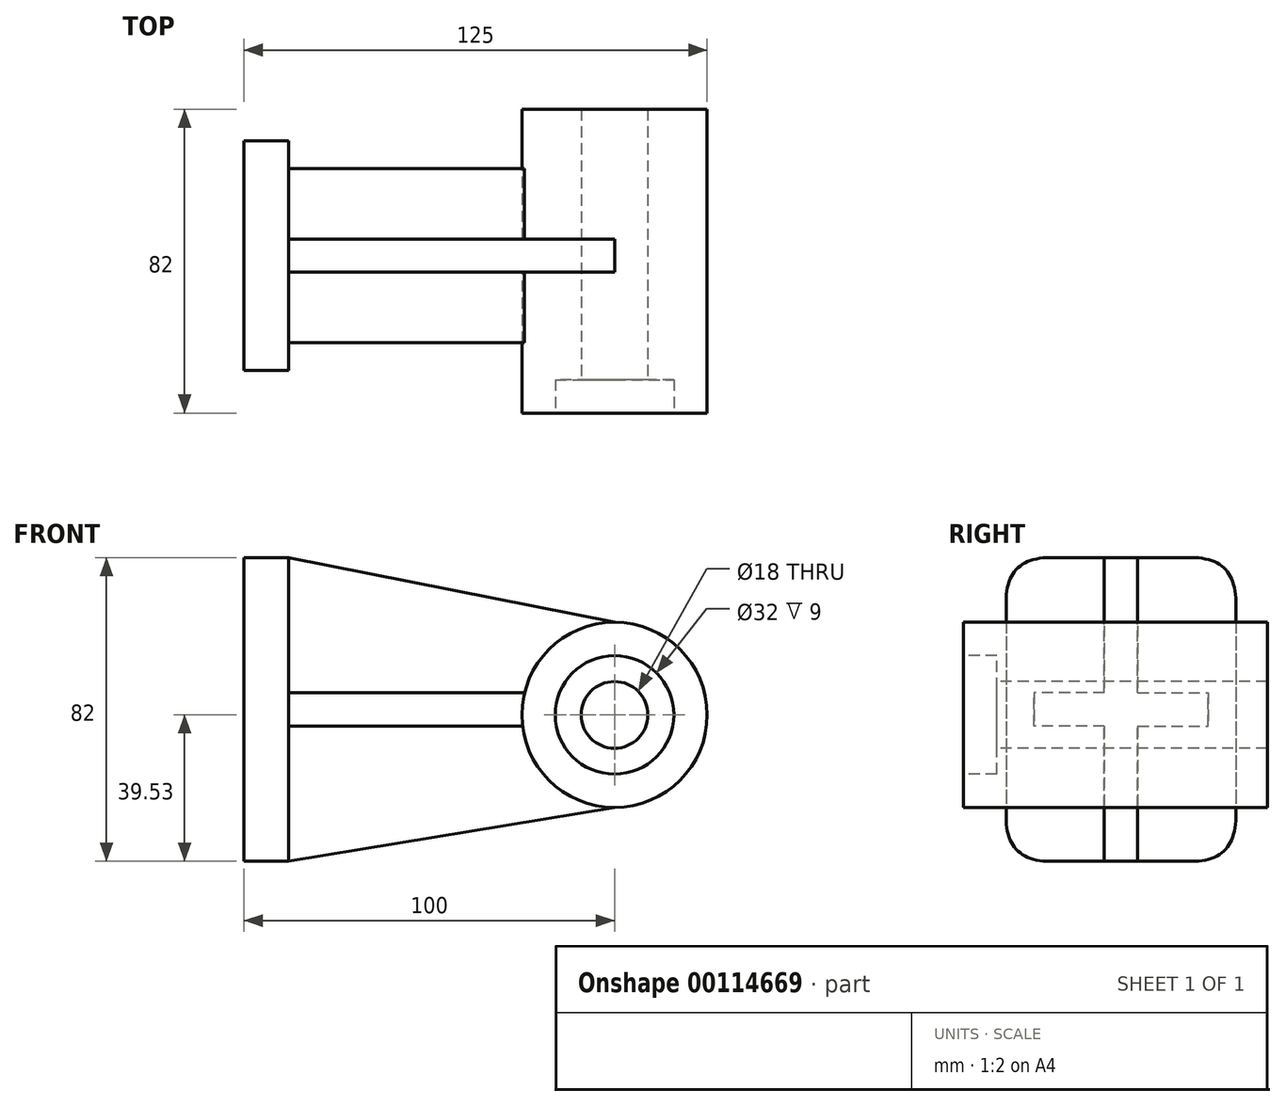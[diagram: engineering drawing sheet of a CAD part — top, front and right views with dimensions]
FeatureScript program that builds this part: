
annotation { "Feature Type Name" : "Feature", "Feature Type Description" : "" }
export const myFeature = defineFeature(function(context is Context, id is Id, definition is map)
    precondition{}
    {
        {
            var Q0;
            Q0=qCreatedBy(makeId("Right.planeOp"),FACE);
            var sketch = newSketch(context, id + "F0", { "sketchPlane" : qUnion([Q0])});
            skLineSegment(sketch, "E0.bottom", {"start": v(31, 42.47) * mm, "end": v(-31, 42.47) * mm});
            skLineSegment(sketch, "E0.top", {"start": v(31, -39.53) * mm, "end": v(-31, -39.53) * mm});
            skLineSegment(sketch, "E0.left", {"start": v(31, 42.47) * mm, "end": v(31, -39.53) * mm});
            skLineSegment(sketch, "E0.right", {"start": v(-31, 42.47) * mm, "end": v(-31, -39.53) * mm});
            skPoint(sketch, "E1", {"position": v(0, 42.47) * mm});
            skSolve(sketch);
        }
        {
            var Q0;
            Q0 = qSketchRegion(id + "F0", true);
            extrude(context, id + "F1", {"entities" : qUnion([Q0]), "depth" : 12 * mm});
        }
        {
            var Q0;
            Q0=makeQuery(id+"F1.opExtrude","SWEPT_EDGE",EDGE,{"disambiguationData":[OSD([sQuery(id+"F0.wireOp",EDGE,"E0.bottom"),sQuery(id+"F0.wireOp",EDGE,"E0.right")])]});
            var Q1;
            Q1=makeQuery(id+"F1.opExtrude","SWEPT_EDGE",EDGE,{"disambiguationData":[OSD([sQuery(id+"F0.wireOp",EDGE,"E0.bottom"),sQuery(id+"F0.wireOp",EDGE,"E0.left")])]});
            var Q2;
            Q2=makeQuery(id+"F1.opExtrude","SWEPT_EDGE",EDGE,{"disambiguationData":[OSD([sQuery(id+"F0.wireOp",EDGE,"E0.top"),sQuery(id+"F0.wireOp",EDGE,"E0.right")])]});
            var Q3;
            Q3=makeQuery(id+"F1.opExtrude","SWEPT_EDGE",EDGE,{"disambiguationData":[OSD([sQuery(id+"F0.wireOp",EDGE,"E0.top"),sQuery(id+"F0.wireOp",EDGE,"E0.left")])]});
            fillet(context, id + "F2", {"entities" : qUnion([Q0, Q1, Q2, Q3]), "radius" : 12 * mm, "tangentPropagation" : true, "rho" : 0.5, "crossSection" : FilletCrossSection.CONIC, "allowEdgeOverflow" : false});
        }
        {
            var Q0;
            Q0=makeQuery(id+"F1.opExtrude","CAP_FACE",FACE,{"disambiguationData":[OSD([sQuery(id+"F0.wireOp",EDGE,"E0.bottom"),sQuery(id+"F0.wireOp",EDGE,"E0.top"),sQuery(id+"F0.wireOp",EDGE,"E0.left"),sQuery(id+"F0.wireOp",EDGE,"E0.right")])],"isStart":false});
            var sketch = newSketch(context, id + "F3", { "sketchPlane" : qUnion([Q0])});
            skLineSegment(sketch, "E2.bottom", {"start": v(4.5, 42.47) * mm, "end": v(-4.5, 42.47) * mm});
            skLineSegment(sketch, "E2.top", {"start": v(4.5, -39.53) * mm, "end": v(-4.5, -39.53) * mm});
            skLineSegment(sketch, "E2.left", {"start": v(4.5, 42.47) * mm, "end": v(4.5, 5.97) * mm});
            skLineSegment(sketch, "E2.right", {"start": v(-4.5, 42.47) * mm, "end": v(-4.5, -39.53) * mm});
            skPoint(sketch, "E3", {"position": v(0, 38.67) * mm});
            skPoint(sketch, "E3.positionSnap0", {"position": v(0, 42.47) * mm});
            skLineSegment(sketch, "E4.bottom", {"start": v(-4.5, 5.97) * mm, "end": v(-23.5, 5.97) * mm});
            skLineSegment(sketch, "E4.top", {"start": v(-4.5, -3.03) * mm, "end": v(-23.5, -3.03) * mm});
            skLineSegment(sketch, "E4.right", {"start": v(-23.5, 5.97) * mm, "end": v(-23.5, -3.03) * mm});
            skPoint(sketch, "E5", {"position": v(-23.5, 1.47) * mm});
            skLineSegment(sketch, "E6.bottom", {"start": v(4.5, 5.97) * mm, "end": v(23.5, 5.97) * mm});
            skLineSegment(sketch, "E6.top", {"start": v(4.5, -3.03) * mm, "end": v(23.5, -3.03) * mm});
            skLineSegment(sketch, "E6.right", {"start": v(23.5, 5.97) * mm, "end": v(23.5, -3.03) * mm});
            skPoint(sketch, "E7", {"position": v(23.5, 1.47) * mm});
            skLineSegment(sketch, "E8.trimOffspring", {"start": v(4.5, -3.03) * mm, "end": v(4.5, -39.53) * mm});
            skSolve(sketch);
        }
        {
            var Q0;
            Q0=qCreatedBy(makeId("Front.planeOp"),FACE);
            var sketch = newSketch(context, id + "F4", { "sketchPlane" : qUnion([Q0])});
            skCircle(sketch, "E9", {"center": v(100, 0) * mm, "radius": 25 * mm});
            skSolve(sketch);
        }
        {
            var Q0;
            Q0 = qSketchRegion(id + "F4", true);
            extrude(context, id + "F5", {"entities" : qUnion([Q0]), "operationType" : NewBodyOperationType.ADD, "depth" : 42.5 * mm, "hasSecondDirection" : true, "secondDirectionOppositeDirection" : true, "secondDirectionDepth" : 39.5 * mm});
        }
        {
            var Q0;
            Q0 = qSketchRegion(id + "F3", true);
            extrude(context, id + "F6", {"entities" : qUnion([Q0]), "operationType" : NewBodyOperationType.ADD, "depth" : 88 * mm});
        }
        {
            var Q0;
            {var subQ0=sQuery(id+"F3.wireOp",EDGE,"E2.right");Q0=makeQuery(id+"F6.opExtrude","SWEPT_FACE",FACE,{"disambiguationData":[OSD([subQ0]),TDD([makeQuery(id+"F3.imprint","IMPRINT",EDGE,{"disambiguationData":[TD([[makeQuery(id+"F3.imprint","INTERSECT",VERTEX,{"derivedFrom":[subQ0,sQuery(id+"F3.wireOp",EDGE,"E4.bottom")]}),1.0]])],"derivedFrom":subQ0})])]});}
            var sketch = newSketch(context, id + "F7", { "sketchPlane" : qUnion([Q0])});
            skPoint(sketch, "E10", {"position": v(100, 25) * mm});
            skPoint(sketch, "E11", {"position": v(12, 42.47) * mm});
            skPoint(sketch, "E12", {"position": v(100, 42.47) * mm});
            skLineSegment(sketch, "E13", {"start": v(12, 42.47) * mm, "end": v(100, 25) * mm});
            skLineSegment(sketch, "E14", {"start": v(100, 42.47) * mm, "end": v(12, 42.47) * mm});
            skLineSegment(sketch, "E15", {"start": v(100, 42.47) * mm, "end": v(100, 25) * mm});
            skSolve(sketch);
        }
        {
            var Q0;
            Q0 = qSketchRegion(id + "F7", true);
            extrude(context, id + "F8", {"entities" : qUnion([Q0]), "operationType" : NewBodyOperationType.REMOVE, "oppositeDirection" : true, "depth" : 25 * mm});
        }
        {
            var Q0;
            {var subQ0=sQuery(id+"F3.wireOp",EDGE,"E2.right");Q0=makeQuery(id+"F6.opExtrude","SWEPT_FACE",FACE,{"disambiguationData":[OSD([subQ0]),TDD([makeQuery(id+"F3.imprint","IMPRINT",EDGE,{"disambiguationData":[TD([[makeQuery(id+"F3.imprint","INTERSECT",VERTEX,{"derivedFrom":[subQ0,sQuery(id+"F3.wireOp",EDGE,"E4.top")]}),-1.0]])],"derivedFrom":subQ0})])]});}
            var sketch = newSketch(context, id + "F9", { "sketchPlane" : qUnion([Q0])});
            skPoint(sketch, "E16", {"position": v(100, -25) * mm});
            skPoint(sketch, "E17", {"position": v(100, -39.53) * mm});
            skLineSegment(sketch, "E18", {"start": v(100, -25) * mm, "end": v(100, -39.53) * mm});
            skPoint(sketch, "E19", {"position": v(12, -39.53) * mm});
            skLineSegment(sketch, "E20", {"start": v(12, -39.53) * mm, "end": v(100, -25) * mm});
            skLineSegment(sketch, "E21", {"start": v(100, -39.53) * mm, "end": v(12, -39.53) * mm});
            skSolve(sketch);
        }
        {
            var Q0;
            Q0 = qSketchRegion(id + "F9", true);
            extrude(context, id + "F10", {"entities" : qUnion([Q0]), "operationType" : NewBodyOperationType.REMOVE, "oppositeDirection" : true, "depth" : 25 * mm});
        }
        {
            var Q0;
            Q0=makeQuery(id+"F5.opExtrude","CAP_FACE",FACE,{"disambiguationData":[OSD([sQuery(id+"F4.wireOp",EDGE,"E9")])],"isStart":false});
            var sketch = newSketch(context, id + "F11", { "sketchPlane" : qUnion([Q0])});
            skPoint(sketch, "E22", {"position": v(100, 0) * mm});
            skSolve(sketch);
        }
        {
            var Q0;
            Q0=sQuery(id+"F11.wireOp",VERTEX,"E22");
            var Q1;
            Q1=makeQuery(id+"F1.opExtrude","SWEPT_BODY",BODY,{"disambiguationData":[OSD([sQuery(id+"F0.wireOp",EDGE,"E0.bottom"),sQuery(id+"F0.wireOp",EDGE,"E0.top"),sQuery(id+"F0.wireOp",EDGE,"E0.left"),sQuery(id+"F0.wireOp",EDGE,"E0.right")])]});
            hole(context, id + "F12", {"style" : HoleStyle.C_BORE, "endStyle" : HoleEndStyle.BLIND, "holeDiameter" : 18 * mm, "cBoreDiameter" : 32 * mm, "cBoreDepth" : 9 * mm, "holeDepth" : 90 * mm, "startFromSketch" : true, "locations" : qUnion([Q0]), "scope" : qUnion([Q1])});
        }
    });
